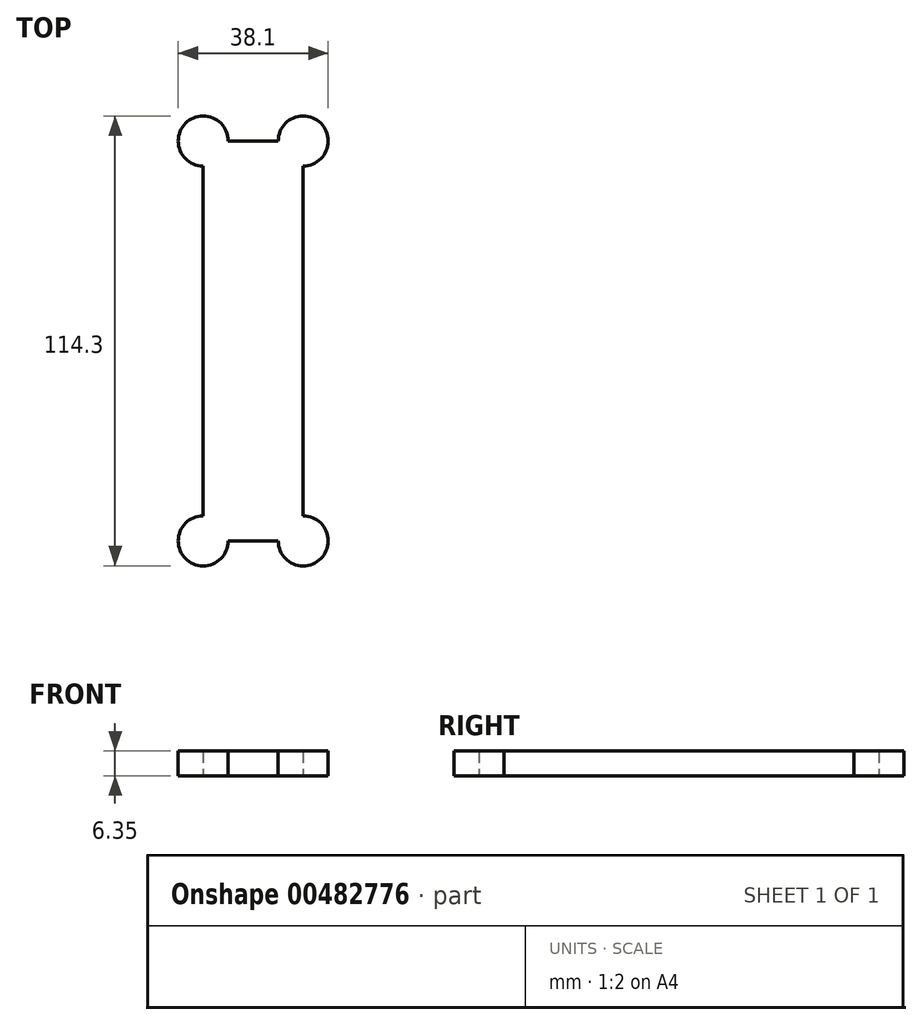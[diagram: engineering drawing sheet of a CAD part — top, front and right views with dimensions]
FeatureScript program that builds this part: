
annotation { "Feature Type Name" : "Feature", "Feature Type Description" : "" }
export const myFeature = defineFeature(function(context is Context, id is Id, definition is map)
    precondition{}
    {
        {
            var Q0;
            Q0=qCreatedBy(makeId("Top.planeOp"),FACE);
            var sketch = newSketch(context, id + "F0", { "sketchPlane" : qUnion([Q0])});
            skLineSegment(sketch, "E0.bottom", {"start": v(127, 127) * mm, "end": v(-127, 127) * mm});
            skLineSegment(sketch, "E0.top", {"start": v(127, -127) * mm, "end": v(-127, -127) * mm});
            skLineSegment(sketch, "E0.left", {"start": v(127, 127) * mm, "end": v(127, -127) * mm});
            skLineSegment(sketch, "E0.right", {"start": v(-127, 127) * mm, "end": v(-127, -127) * mm});
            skPoint(sketch, "E0.middle", {"position": v(0, 0) * mm});
            skSolve(sketch);
        }
        {
            var Q0;
            Q0 = qSketchRegion(id + "F0", true);
            var Q1;
            Q1=makeQuery(id+"F0.imprint","IMPRINT",FACE,{"disambiguationData":[TD([[makeQuery(id+"F0.imprint","IMPRINT",EDGE,{"derivedFrom":sQuery(id+"F0.wireOp",EDGE,"E0.bottom")}),1.0]])]});
            extrude(context, id + "F1", {"entities" : qUnion([Q0, Q1]), "depth" : 6.35 * mm, "offsetDistance" : 25.4 * mm});
        }
        {
            var Q0;
            Q0=makeQuery(id+"F1.opExtrude","CAP_FACE",FACE,{"disambiguationData":[OSD([sQuery(id+"F0.wireOp",EDGE,"E0.bottom"),sQuery(id+"F0.wireOp",EDGE,"E0.top"),sQuery(id+"F0.wireOp",EDGE,"E0.left"),sQuery(id+"F0.wireOp",EDGE,"E0.right")])],"isStart":true});
            var sketch = newSketch(context, id + "F2", { "sketchPlane" : qUnion([Q0])});
            skLineSegment(sketch, "E1.bottom", {"start": v(-94.2, 101.6) * mm, "end": v(-81.5, 101.6) * mm});
            skLineSegment(sketch, "E1.top", {"start": v(-94.2, 0) * mm, "end": v(-81.5, 0) * mm});
            skLineSegment(sketch, "E1.left", {"start": v(-100.55, 95.25) * mm, "end": v(-100.55, 6.35) * mm});
            skLineSegment(sketch, "E1.right", {"start": v(-75.15, 95.25) * mm, "end": v(-75.15, 6.35) * mm});
            skArc(sketch, "E2", {"start": v(-75.15, 95.25) * mm, "mid": v(-70.66, 106.1) * mm, "end": v(-81.5, 101.6) * mm});
            skArc(sketch, "E3", {"start": v(-100.55, 6.35) * mm, "mid": v(-105.04, -4.5) * mm, "end": v(-94.2, 0) * mm});
            skArc(sketch, "E4", {"start": v(-75.15, 6.35) * mm, "mid": v(-70.66, -4.5) * mm, "end": v(-81.5, 0) * mm});
            skPoint(sketch, "E5.start.orphan", {"position": v(-87.85, 101.6) * mm});
            skArc(sketch, "E6", {"start": v(-100.55, 95.25) * mm, "mid": v(-105.04, 106.1) * mm, "end": v(-94.2, 101.6) * mm});
            skSolve(sketch);
        }
        {
            var Q0;
            Q0=makeQuery(id+"F2.imprint","IMPRINT",FACE,{"disambiguationData":[TD([[makeQuery(id+"F2.imprint","IMPRINT",EDGE,{"derivedFrom":sQuery(id+"F2.wireOp",EDGE,"E1.bottom")}),1.0]])]});
            extrude(context, id + "F3", {"entities" : qUnion([Q0]), "operationType" : NewBodyOperationType.REMOVE, "oppositeDirection" : true, "depth" : 25.4 * mm, "offsetDistance" : 25.4 * mm});
        }
    });
